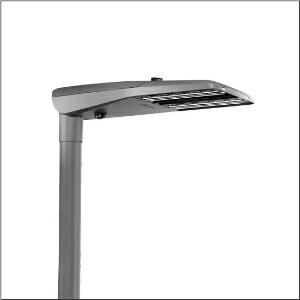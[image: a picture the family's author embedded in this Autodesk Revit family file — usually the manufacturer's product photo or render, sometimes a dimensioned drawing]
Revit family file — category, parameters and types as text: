
# Revit family: streetlight_sl_11_iq_midi___pc-r_5xc3f11y08me_2da3
name_source: partatom
category: Lighting Fixtures
units: mm (PartAtom-declared; Revit-internal decimal feet)

## family parameters
Cut with Voids When Loaded = No
Host = Face
Light Source = No
Part Type = Normal
Room Calculation Point = No
Round Connector Dimension = Use Diameter
Shared = No

## types (1)
- --- (1 x LED, 9610 lm, 123.4 W, 1800K)
    Apparent Load = 123 VA
    CIE Flux Codes = 37 73 96 100 100
    Color Rendering = 70
    Color Temperature = 1800K
    Default Elevation = 1800 mm  [stored 5.90551 ft]
    Description = Streetlight SL 11 iQ midi, mast luminaire, primary light control with 3 zone facetted reflector, of plastic, silver coated, highly specular, primary optical cover: cover, of PMMA, transparent, light distribution: PC-R, light emission: direct distribution, primary light characteristic: asymmetric, right, installation type: post-top, side-entry, LED, High Power LED, rated luminous flux: 9.610lm, luminous efficacy: 78lm/W, light colour: 718, colour temperature: 1800K, control: presetting dimming logarithmic, Street-Remote, Auto-Match, Temp-Guard, Lumen-Switch, Night-Set, Smart-Wire, Light-Fading, Desk-Remote (wireless, voltage-free reading and setting of iQ features in the workshop via application-optimized NFC function/RFID function), optimised constant luminous flux control (CLO 2.0), with cable H07RN-F 5x 1.5mm², mains connection: 230..240V, AC, 50/60Hz, connection cable pre-assembled, cable length: 12,5m, start of lifetime: 123W, end of service life: 131W, reduction: 54W, luminaire housing, of diecast aluminium, powder-coated, Siteco® metallic grey (DB 702S), please order mast flange separately, inclination adjustable without tools: 0°, 5°, 10°, 15° (post-top) | 0°, -5°, -10°, -15° (side-entry), sealing non-destructively replaceable, multi-level sealing system, length: 780mm, width: 376mm, height: 118mm, mast flange for spigot size: 42mm (side-entry): 5XC10008XM4, 60/48mm (side-entry/post-top): 5XC10108XM2, 76/60mm (side-entry/post-top): 5XC10108XM1, equipment: Power, Smart Interface below and above, protection rating (complete): IP66, insulation class (complete): insulation class II (safety insulation), certification: CE, ENEC, VDE, UKCA, impact resistance: IK09, permissible operating ambient temperature for outdoor applications: -25..+50°C, standard-compliant lighting for roads and squares, Environmental Product Declaration (EPD) tested and certified by an independent institute, packaging unit: 1 piece

Light Distribution: PC-R
    Height = 118 mm
    Lamp = 1 x LED
    Lamp Light Flux = 9610 lm
    Lamp Power = 123.4 W
    Lamp count = 1
    Length = 780 mm
    Luminous efficacy = 78 lm/W
    Manufacturer = Siteco
    ModVariant = No
    Model = 5XC3F11Y08ME
    Number of Poles = 1
    OnlyDefault = Yes
    Power Factor = 1
    Product Name = Streetlight SL 11 iQ midi | PC-R
    Product group = mast luminaire | pylon top
    ProductGroupID = 6100
    Protection Class = Protection class II
    Protection Degree = IP 66
    RLX_Detail_Level = 1
    RLX_Emergency_Light_Flux = 0 lm
    RLX_Emergency_Type = 0
    RLX_Emergency_Type_DB = No
    RlxData = <blob elided: 73261 chars, md5=429f00ed>
    Socket = socket
    Standby Power = 0 W
    System Light Flux = 9610 lm
    System Power = 123 W
    Type Comments = factory setting: luminous flux: 100 % | dim-lin: 254 | 553 mA
    Type Image = l_1004429.jpg
    URL = http://relux.com
    VarID = @adj_058109
    Voltage = 0 V
    Weight = 0.00 kg
    Width = 376 mm

note: [stored X ft] marks values corroborated as IEEE doubles in the binary element streams (Revit-internal decimal feet)

## geometry (parser evidence)
native form markers: Blend x4, Sweep x10
no freeform markers — native parametric forms only
